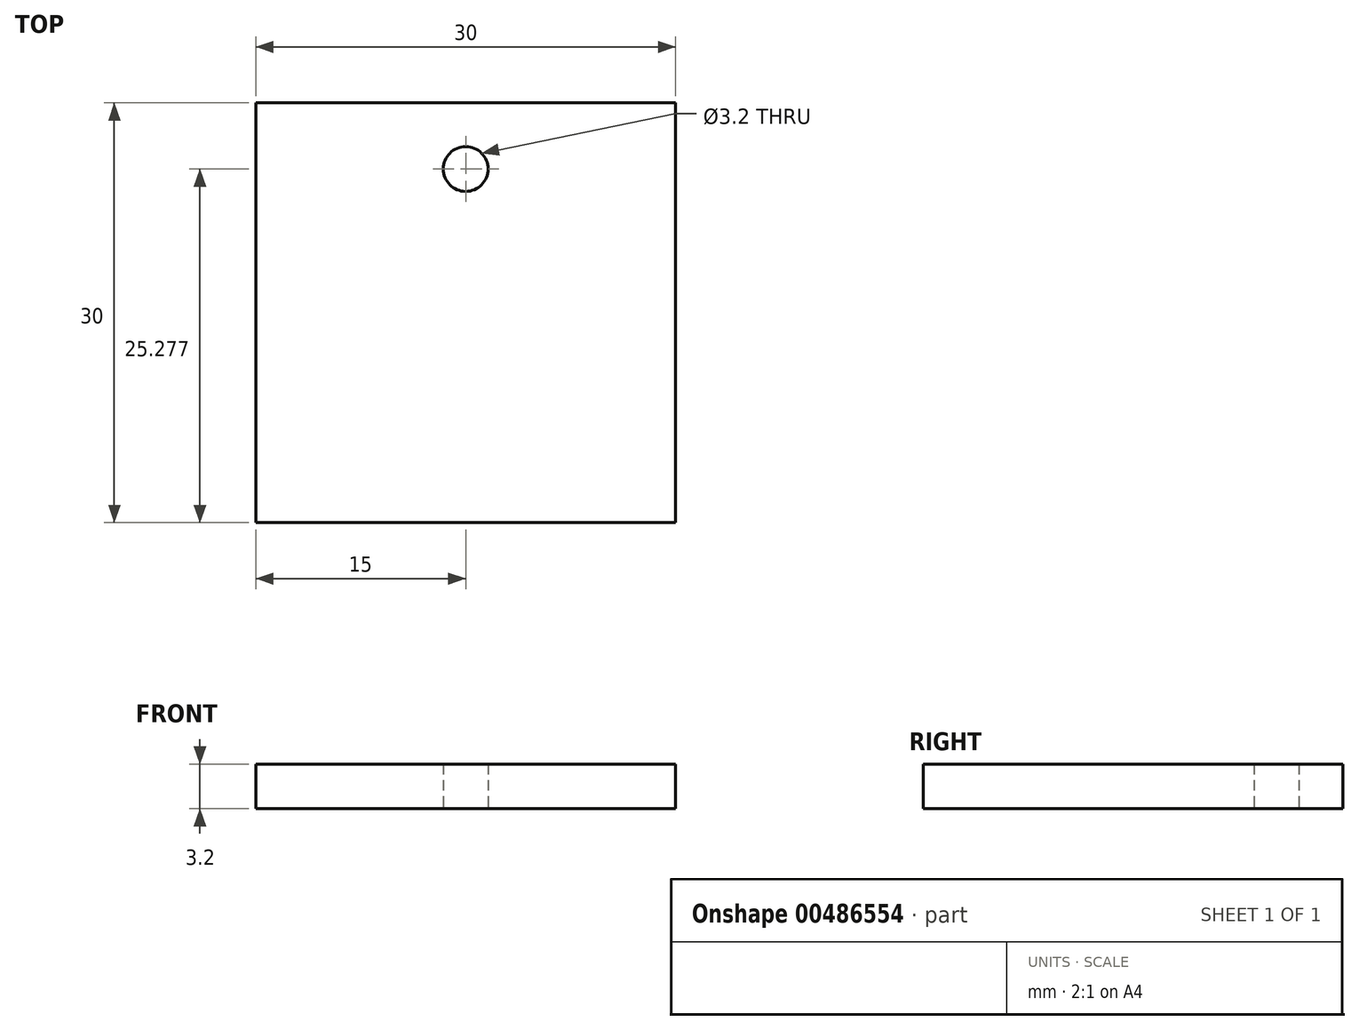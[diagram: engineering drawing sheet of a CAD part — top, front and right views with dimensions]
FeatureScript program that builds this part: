
annotation { "Feature Type Name" : "Feature", "Feature Type Description" : "" }
export const myFeature = defineFeature(function(context is Context, id is Id, definition is map)
    precondition{}
    {
        {
            var Q0;
            Q0=qCreatedBy(makeId("Top.planeOp"),FACE);
            var sketch = newSketch(context, id + "F0", { "sketchPlane" : qUnion([Q0])});
            skLineSegment(sketch, "E0.bottom", {"start": v(-15, 15) * mm, "end": v(15, 15) * mm});
            skLineSegment(sketch, "E0.top", {"start": v(-15, -15) * mm, "end": v(15, -15) * mm});
            skLineSegment(sketch, "E0.left", {"start": v(-15, 15) * mm, "end": v(-15, -15) * mm});
            skLineSegment(sketch, "E0.right", {"start": v(15, 15) * mm, "end": v(15, -15) * mm});
            skPoint(sketch, "E0.middle", {"position": v(0, 0) * mm});
            skCircle(sketch, "E1", {"center": v(0, 10.28) * mm, "radius": 1.6 * mm});
            skSolve(sketch);
        }
        {
            var Q0;
            Q0=makeQuery(id+"F0.imprint","IMPRINT",FACE,{"disambiguationData":[TD([[makeQuery(id+"F0.imprint","IMPRINT",EDGE,{"derivedFrom":sQuery(id+"F0.wireOp",EDGE,"E0.bottom")}),-1.0]])]});
            extrude(context, id + "F1", {"entities" : qUnion([Q0]), "depth" : 3.2 * mm, "offsetDistance" : 25 * mm});
        }
        {
            var Q0;
            Q0=makeQuery(id+"F0.imprint","IMPRINT",FACE,{"disambiguationData":[TD([[makeQuery(id+"F0.imprint","IMPRINT",EDGE,{"derivedFrom":sQuery(id+"F0.wireOp",EDGE,"E0.bottom")}),-1.0]])]});
            extrude(context, id + "F2", {"entities" : qUnion([Q0]), "operationType" : NewBodyOperationType.ADD, "depth" : 3.2 * mm, "offsetDistance" : 25 * mm});
        }
    });
